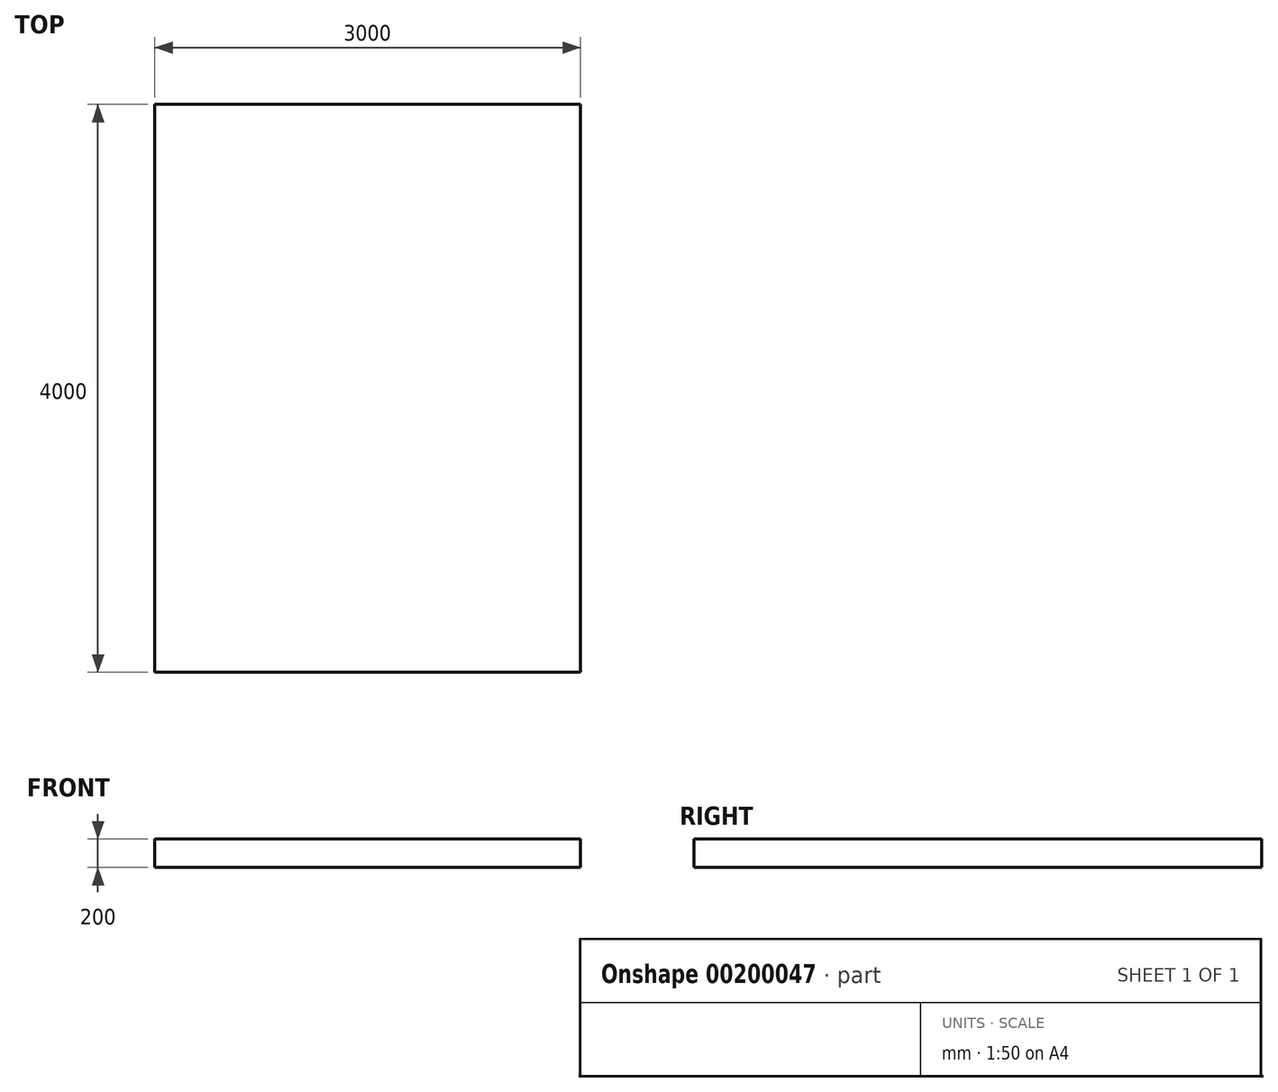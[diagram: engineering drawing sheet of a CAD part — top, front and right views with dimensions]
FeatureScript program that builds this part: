
annotation { "Feature Type Name" : "Feature", "Feature Type Description" : "" }
export const myFeature = defineFeature(function(context is Context, id is Id, definition is map)
    precondition{}
    {
        {
            var Q0;
            Q0=qCreatedBy(makeId("Top.planeOp"),FACE);
            var sketch = newSketch(context, id + "F0", { "sketchPlane" : qUnion([Q0])});
            skLineSegment(sketch, "E0.bottom", {"start": v(-1500, 2000) * mm, "end": v(1500, 2000) * mm});
            skLineSegment(sketch, "E0.top", {"start": v(-1500, -2000) * mm, "end": v(1500, -2000) * mm});
            skLineSegment(sketch, "E0.left", {"start": v(-1500, 2000) * mm, "end": v(-1500, -2000) * mm});
            skLineSegment(sketch, "E0.right", {"start": v(1500, 2000) * mm, "end": v(1500, -2000) * mm});
            skSolve(sketch);
        }
        {
            var Q0;
            Q0 = qSketchRegion(id + "F0", true);
            extrude(context, id + "F1", {"entities" : qUnion([Q0]), "depth" : 200 * mm});
        }
    });
